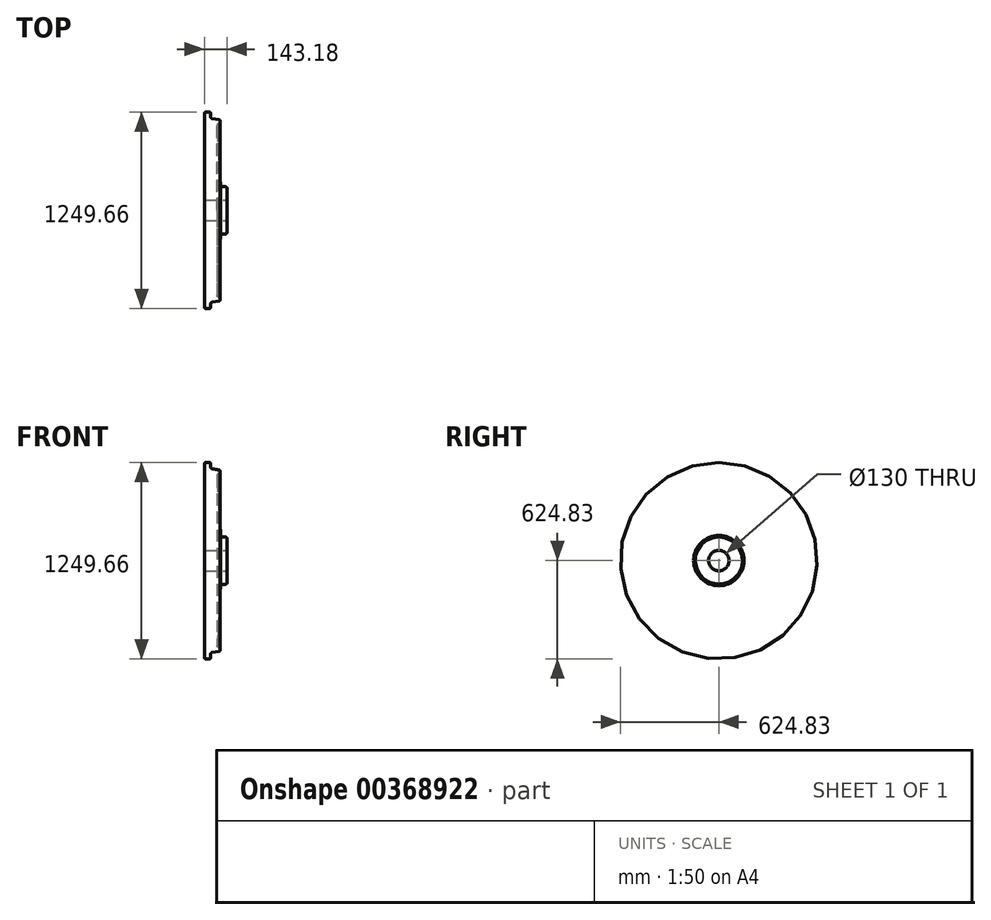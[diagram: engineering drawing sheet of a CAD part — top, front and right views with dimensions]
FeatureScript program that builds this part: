
annotation { "Feature Type Name" : "Feature", "Feature Type Description" : "" }
export const myFeature = defineFeature(function(context is Context, id is Id, definition is map)
    precondition{}
    {
        {
            var Q0;
            Q0=qCreatedBy(makeId("Front.planeOp"),FACE);
            var sketch = newSketch(context, id + "F0", { "sketchPlane" : qUnion([Q0])});
            skLineSegment(sketch, "E0.bottom", {"start": v(-44.27, 624.7) * mm, "end": v(-24.27, 624.83) * mm});
            skLineSegment(sketch, "E0.left", {"start": v(-54.2, 614.63) * mm, "end": v(-50, 0) * mm});
            skLineSegment(sketch, "E0.right", {"start": v(46.13, 566.22) * mm, "end": v(46.16, 562.5) * mm});
            skPoint(sketch, "E0.middle", {"position": v(0, 0) * mm});
            skPoint(sketch, "E1.visualSharp", {"position": v(-54.27, 624.63) * mm});
            skArc(sketch, "E1.filletArc", {"start": v(-44.27, 624.7) * mm, "mid": v(-51.32, 621.72) * mm, "end": v(-54.2, 614.63) * mm});
            skLineSegment(sketch, "E2", {"start": v(-14.2, 614.9) * mm, "end": v(-14.06, 593.17) * mm});
            skLineSegment(sketch, "E3", {"start": v(-5.72, 583.38) * mm, "end": v(37.8, 576.01) * mm});
            skPoint(sketch, "E4.newPointA", {"position": v(45.73, 625.31) * mm});
            skPoint(sketch, "E4.newPointB", {"position": v(-14.27, 624.78) * mm});
            skArc(sketch, "E4.filletArc", {"start": v(-14.2, 614.9) * mm, "mid": v(-17.18, 621.95) * mm, "end": v(-24.27, 624.83) * mm});
            skPoint(sketch, "E5.visualSharp", {"position": v(-14, 584.78) * mm});
            skArc(sketch, "E5.filletArc", {"start": v(-14.06, 593.17) * mm, "mid": v(-11.67, 586.76) * mm, "end": v(-5.72, 583.38) * mm});
            skArc(sketch, "E6.filletArc", {"start": v(46.13, 566.22) * mm, "mid": v(43.75, 572.63) * mm, "end": v(37.8, 576.01) * mm});
            skLineSegment(sketch, "E7", {"start": v(-50, 0) * mm, "end": v(50, 0) * mm});
            skPoint(sketch, "E0.top.end.orphan", {"position": v(54.27, -624.63) * mm});
            skPoint(sketch, "E0.top.start.orphan", {"position": v(-45.73, -625.31) * mm});
            skLineSegment(sketch, "E8", {"start": v(58.98, 149.8) * mm, "end": v(78.9, 149.93) * mm});
            skLineSegment(sketch, "E9", {"start": v(88.98, 139.93) * mm, "end": v(88.98, 0) * mm});
            skLineSegment(sketch, "E10", {"start": v(88.98, 0) * mm, "end": v(50, 0) * mm});
            skPoint(sketch, "E11.visualSharp", {"position": v(48.98, 149.73) * mm});
            skArc(sketch, "E11.filletArc", {"start": v(48.9, 159.73) * mm, "mid": v(51.89, 152.68) * mm, "end": v(58.98, 149.8) * mm});
            skPoint(sketch, "E12.visualSharp", {"position": v(88.98, 150) * mm});
            skArc(sketch, "E12.filletArc", {"start": v(88.98, 139.93) * mm, "mid": v(86.02, 147.03) * mm, "end": v(78.9, 149.93) * mm});
            skLineSegment(sketch, "E13", {"start": v(39.84, 553.13) * mm, "end": v(32.92, 550.39) * mm});
            skLineSegment(sketch, "E14", {"start": v(26.63, 540.5) * mm, "end": v(48.9, 159.73) * mm});
            skPoint(sketch, "E15.newPointB", {"position": v(46.2, 555.65) * mm});
            skArc(sketch, "E15.filletArc", {"start": v(39.84, 553.13) * mm, "mid": v(44.45, 556.83) * mm, "end": v(46.16, 562.5) * mm});
            skPoint(sketch, "E16.visualSharp", {"position": v(26.2, 547.72) * mm});
            skArc(sketch, "E16.filletArc", {"start": v(32.92, 550.39) * mm, "mid": v(28.18, 546.47) * mm, "end": v(26.63, 540.5) * mm});
            skSolve(sketch);
        }
        {
            var Q0;
            Q0=qCreatedBy(makeId("Right.planeOp"),FACE);
            var sketch = newSketch(context, id + "F1", { "sketchPlane" : qUnion([Q0])});
            skCircle(sketch, "E17", {"center": v(0, 0) * mm, "radius": 39.93 * mm, "construction": true});
            skSolve(sketch);
        }
        {
            var Q0;
            Q0=makeQuery(id+"F0.imprint","IMPRINT",FACE,{"disambiguationData":[TD([[makeQuery(id+"F0.imprint","IMPRINT",EDGE,{"derivedFrom":sQuery(id+"F0.wireOp",EDGE,"E0.bottom")}),-1.0]])]});
            var Q1;
            Q1=sQuery(id+"F1.wireOp",EDGE,"E17");
            revolve(context, id + "F2", {"surfaceOperationType" : NewSurfaceOperationType.NEW, "entities" : qUnion([Q0]), "axis" : qUnion([Q1]), "revolveType" : RevolveType.FULL});
        }
        {
            var Q0;
            Q0=makeQuery(id+"F2.opRevolve","SWEPT_FACE",FACE,{"disambiguationData":[OSD([sQuery(id+"F0.wireOp",EDGE,"E9")])]});
            var sketch = newSketch(context, id + "F3", { "sketchPlane" : qUnion([Q0])});
            skPoint(sketch, "E18", {"position": v(0, 0) * mm});
            skSolve(sketch);
        }
        {
            var Q0;
            Q0=sQuery(id+"F3.wireOp",VERTEX,"E18");
            var Q1;
            Q1=makeQuery(id+"F2.opRevolve","SWEPT_BODY",BODY,{"disambiguationData":[OSD([sQuery(id+"F0.wireOp",EDGE,"E0.bottom"),sQuery(id+"F0.wireOp",EDGE,"E0.left"),sQuery(id+"F0.wireOp",EDGE,"E0.right"),sQuery(id+"F0.wireOp",EDGE,"E1.filletArc"),sQuery(id+"F0.wireOp",EDGE,"E2"),sQuery(id+"F0.wireOp",EDGE,"E3"),sQuery(id+"F0.wireOp",EDGE,"E4.filletArc"),sQuery(id+"F0.wireOp",EDGE,"E5.filletArc"),sQuery(id+"F0.wireOp",EDGE,"E6.filletArc"),sQuery(id+"F0.wireOp",EDGE,"E7"),sQuery(id+"F0.wireOp",EDGE,"E8"),sQuery(id+"F0.wireOp",EDGE,"E9"),sQuery(id+"F0.wireOp",EDGE,"E10"),sQuery(id+"F0.wireOp",EDGE,"E11.filletArc"),sQuery(id+"F0.wireOp",EDGE,"E12.filletArc"),sQuery(id+"F0.wireOp",EDGE,"E13"),sQuery(id+"F0.wireOp",EDGE,"E14"),sQuery(id+"F0.wireOp",EDGE,"E15.filletArc"),sQuery(id+"F0.wireOp",EDGE,"E16.filletArc")])]});
            hole(context, id + "F4", {"style" : HoleStyle.SIMPLE, "endStyle" : HoleEndStyle.THROUGH, "holeDiameter" : 130 * mm, "majorDiameter" : 5 * mm, "isTappedThrough" : true, "tappedDepth" : 12 * mm, "tapClearance" : 3, "locations" : qUnion([Q0]), "scope" : qUnion([Q1])});
        }
    });
